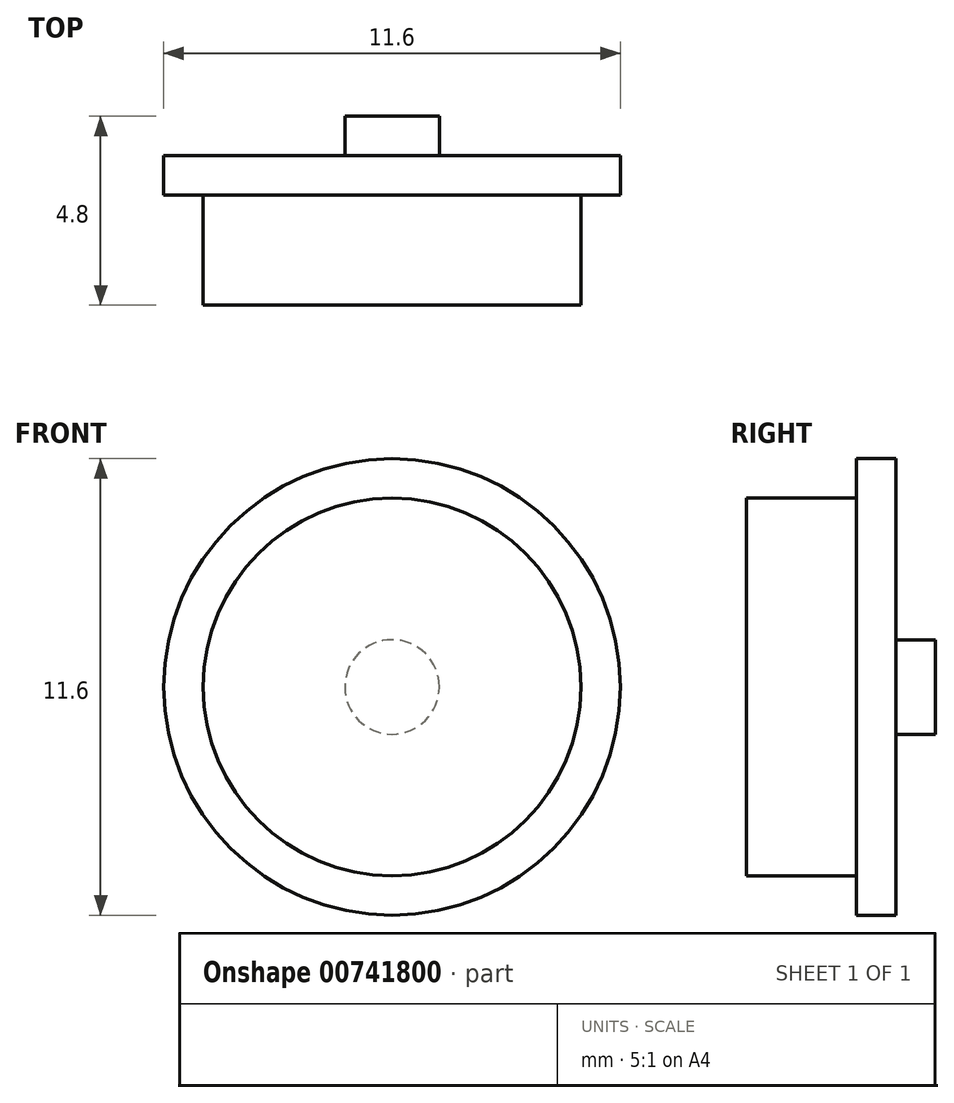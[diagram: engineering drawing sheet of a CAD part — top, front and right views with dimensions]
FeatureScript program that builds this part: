
annotation { "Feature Type Name" : "Feature", "Feature Type Description" : "" }
export const myFeature = defineFeature(function(context is Context, id is Id, definition is map)
    precondition{}
    {
        {
            var Q0;
            Q0=qCreatedBy(makeId("Front.planeOp"),FACE);
            var sketch = newSketch(context, id + "F0", { "sketchPlane" : qUnion([Q0])});
            skCircle(sketch, "E0", {"center": v(0, 0) * mm, "radius": 4.8 * mm});
            skCircle(sketch, "E1.0", {"center": v(0, 0) * mm, "radius": 5.8 * mm});
            skSolve(sketch);
        }
        {
            var Q0;
            Q0=makeQuery(id+"F0.imprint","IMPRINT",FACE,{"disambiguationData":[TD([[makeQuery(id+"F0.imprint","IMPRINT",EDGE,{"derivedFrom":sQuery(id+"F0.wireOp",EDGE,"E0")}),-1.0]])]});
            var Q1;
            Q1=makeQuery(id+"F0.imprint","IMPRINT",FACE,{"disambiguationData":[TD([[makeQuery(id+"F0.imprint","IMPRINT",EDGE,{"derivedFrom":sQuery(id+"F0.wireOp",EDGE,"E0")}),1.0]])]});
            extrude(context, id + "F1", {"entities" : qUnion([Q0, Q1]), "depth" : 1 * mm, "offsetDistance" : 25 * mm});
        }
        {
            var Q0;
            Q0=makeQuery(id+"F0.imprint","IMPRINT",FACE,{"disambiguationData":[TD([[makeQuery(id+"F0.imprint","IMPRINT",EDGE,{"derivedFrom":sQuery(id+"F0.wireOp",EDGE,"E0")}),1.0]])]});
            extrude(context, id + "F2", {"entities" : qUnion([Q0]), "operationType" : NewBodyOperationType.ADD, "depth" : 3.8 * mm, "offsetDistance" : 25 * mm});
        }
        {
            var Q0;
            Q0=makeQuery(id+"F0.imprint","IMPRINT",FACE,{"disambiguationData":[TD([[makeQuery(id+"F0.imprint","IMPRINT",EDGE,{"derivedFrom":sQuery(id+"F0.wireOp",EDGE,"E0")}),1.0]])]});
            var sketch = newSketch(context, id + "F3", { "sketchPlane" : qUnion([Q0])});
            skCircle(sketch, "E2", {"center": v(0, 0) * mm, "radius": 1.2 * mm});
            skSolve(sketch);
        }
        {
            var Q0;
            Q0=makeQuery(id+"F3.imprint","IMPRINT",FACE,{"disambiguationData":[TD([[makeQuery(id+"F3.imprint","IMPRINT",EDGE,{"derivedFrom":sQuery(id+"F3.wireOp",EDGE,"E2")}),1.0]])]});
            extrude(context, id + "F4", {"entities" : qUnion([Q0]), "operationType" : NewBodyOperationType.ADD, "oppositeDirection" : true, "depth" : 1 * mm, "offsetDistance" : 25 * mm});
        }
    });
